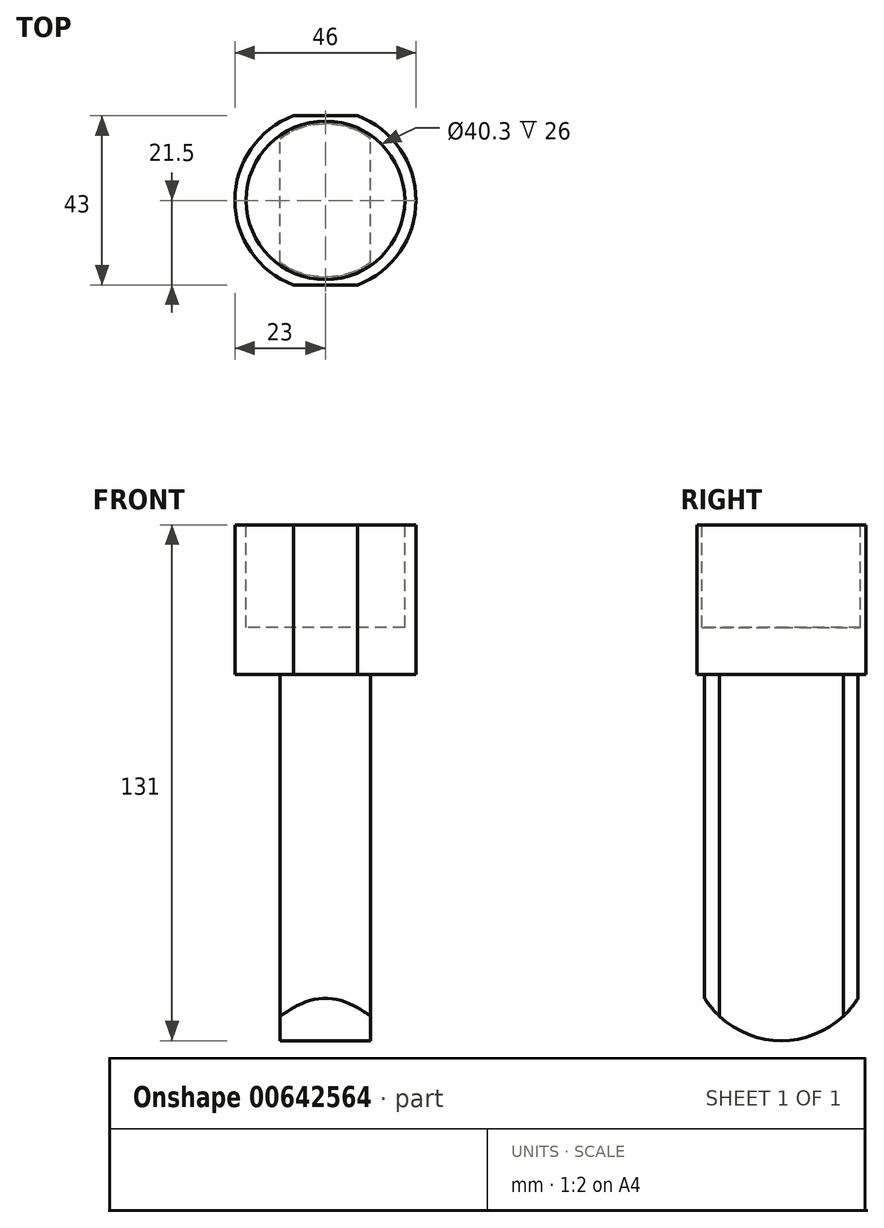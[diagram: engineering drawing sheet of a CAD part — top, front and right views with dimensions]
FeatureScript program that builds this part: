
annotation { "Feature Type Name" : "Feature", "Feature Type Description" : "" }
export const myFeature = defineFeature(function(context is Context, id is Id, definition is map)
    precondition{}
    {
        {
            var Q0;
            Q0=qCreatedBy(makeId("Top.planeOp"),FACE);
            var sketch = newSketch(context, id + "F0", { "sketchPlane" : qUnion([Q0])});
            skArc(sketch, "E0", {"start": v(-8.17, 21.5) * mm, "mid": v(-23, 0) * mm, "end": v(-8.17, -21.5) * mm});
            skLineSegment(sketch, "E1", {"start": v(-8.17, 21.5) * mm, "end": v(8.17, 21.5) * mm});
            skLineSegment(sketch, "E2.MirrorCS", {"start": v(-8.17, -21.5) * mm, "end": v(8.17, -21.5) * mm});
            skArc(sketch, "E3.trimOffspring", {"start": v(8.17, -21.5) * mm, "mid": v(23, 0) * mm, "end": v(8.17, 21.5) * mm});
            skSolve(sketch);
        }
        {
            var Q0;
            Q0 = qSketchRegion(id + "F0", true);
            extrude(context, id + "F1", {"entities" : qUnion([Q0]), "depth" : 38 * mm, "offsetDistance" : 25 * mm});
        }
        {
            var Q0;
            Q0=makeQuery(id+"F1.opExtrude","CAP_FACE",FACE,{"disambiguationData":[OSD([sQuery(id+"F0.wireOp",EDGE,"E0"),sQuery(id+"F0.wireOp",EDGE,"E1"),sQuery(id+"F0.wireOp",EDGE,"E2.MirrorCS"),sQuery(id+"F0.wireOp",EDGE,"E3.trimOffspring")])],"isStart":false});
            var sketch = newSketch(context, id + "F2", { "sketchPlane" : qUnion([Q0])});
            skCircle(sketch, "E4", {"center": v(0, 0) * mm, "radius": 20.15 * mm});
            skSolve(sketch);
        }
        {
            var Q0;
            Q0 = qSketchRegion(id + "F2", true);
            extrude(context, id + "F3", {"entities" : qUnion([Q0]), "operationType" : NewBodyOperationType.REMOVE, "oppositeDirection" : true, "depth" : 26 * mm, "offsetDistance" : 25 * mm});
        }
        {
            var Q0;
            Q0=makeQuery(id+"F1.opExtrude","CAP_FACE",FACE,{"disambiguationData":[OSD([sQuery(id+"F0.wireOp",EDGE,"E0"),sQuery(id+"F0.wireOp",EDGE,"E1"),sQuery(id+"F0.wireOp",EDGE,"E2.MirrorCS"),sQuery(id+"F0.wireOp",EDGE,"E3.trimOffspring")])],"isStart":true});
            var sketch = newSketch(context, id + "F4", { "sketchPlane" : qUnion([Q0])});
            skArc(sketch, "E5", {"start": v(-11.5, -15.75) * mm, "mid": v(0, -19.5) * mm, "end": v(11.5, -15.75) * mm});
            skLineSegment(sketch, "E6", {"start": v(-11.5, 15.75) * mm, "end": v(-11.5, -15.75) * mm});
            skLineSegment(sketch, "E7.MirrorCS", {"start": v(11.5, 15.75) * mm, "end": v(11.5, -15.75) * mm});
            skArc(sketch, "E8.trimOffspring", {"start": v(11.5, 15.75) * mm, "mid": v(0, 19.5) * mm, "end": v(-11.5, 15.75) * mm});
            skSolve(sketch);
        }
        {
            var Q0;
            Q0 = qSketchRegion(id + "F4", true);
            extrude(context, id + "F5", {"entities" : qUnion([Q0]), "operationType" : NewBodyOperationType.ADD, "depth" : 93 * mm, "offsetDistance" : 25 * mm});
        }
        {
            var Q0;
            Q0=makeQuery(id+"F5.opExtrude","SWEPT_FACE",FACE,{"disambiguationData":[OSD([sQuery(id+"F4.wireOp",EDGE,"E7.MirrorCS")])]});
            var sketch = newSketch(context, id + "F6", { "sketchPlane" : qUnion([Q0])});
            skArc(sketch, "E9", {"start": v(-23, -70) * mm, "mid": v(0, -93) * mm, "end": v(23, -70) * mm});
            skLineSegment(sketch, "E10", {"start": v(0, -70) * mm, "end": v(23, -70) * mm});
            skLineSegment(sketch, "E11", {"start": v(23, -70) * mm, "end": v(-23, -70) * mm});
            skLineSegment(sketch, "E12", {"start": v(-23, -70) * mm, "end": v(-43.1, -112.95) * mm});
            skLineSegment(sketch, "E13", {"start": v(-43.1, -112.95) * mm, "end": v(34.32, -112.95) * mm});
            skLineSegment(sketch, "E14", {"start": v(34.32, -112.95) * mm, "end": v(23, -70) * mm});
            skSolve(sketch);
        }
        {
            var Q0;
            {var subQ0=sQuery(id+"F6.wireOp",EDGE,"E12");Q0=makeQuery(id+"F6.imprint","IMPRINT",FACE,{"disambiguationData":[TD([[makeQuery(id+"F6.imprint","IMPRINT",EDGE,{"derivedFrom":subQ0}),1.0]])]});}
            var Q1;
            {var subQ0=sQuery(id+"F6.wireOp",EDGE,"E9");var subQ1=sQuery(id+"F4.wireOp",EDGE,"E7.MirrorCS");var subQ2=makeQuery(id+"F5.opExtrude","CAP_EDGE",EDGE,{"disambiguationData":[OSD([subQ1])],"isStart":false});var subQ3=makeQuery(id+"F6.imprint","INTERSECT",VERTEX,{"derivedFrom":[subQ2,subQ0]});Q1=makeQuery(id+"F6.imprint","IMPRINT",FACE,{"disambiguationData":[TD([[makeQuery(id+"F6.imprint","IMPRINT",EDGE,{"disambiguationData":[TD([[subQ3,-1.0]])],"derivedFrom":subQ0}),-1.0]])]});}
            var Q2;
            {var subQ0=sQuery(id+"F6.wireOp",EDGE,"E9");var subQ1=sQuery(id+"F4.wireOp",EDGE,"E7.MirrorCS");var subQ4=makeQuery(id+"F5.opExtrude","CAP_EDGE",EDGE,{"disambiguationData":[OSD([subQ1])],"isStart":false});var subQ5=makeQuery(id+"F6.imprint","INTERSECT",VERTEX,{"derivedFrom":[subQ4,subQ0]});Q2=makeQuery(id+"F6.imprint","IMPRINT",FACE,{"disambiguationData":[TD([[makeQuery(id+"F6.imprint","IMPRINT",EDGE,{"disambiguationData":[TD([[subQ5,1.0]])],"derivedFrom":subQ0}),-1.0]])]});}
            extrude(context, id + "F7", {"entities" : qUnion([Q0, Q1, Q2]), "operationType" : NewBodyOperationType.REMOVE, "endBound" : BoundingType.THROUGH_ALL, "oppositeDirection" : true, "depth" : 25 * mm, "offsetDistance" : 25 * mm});
        }
    });
